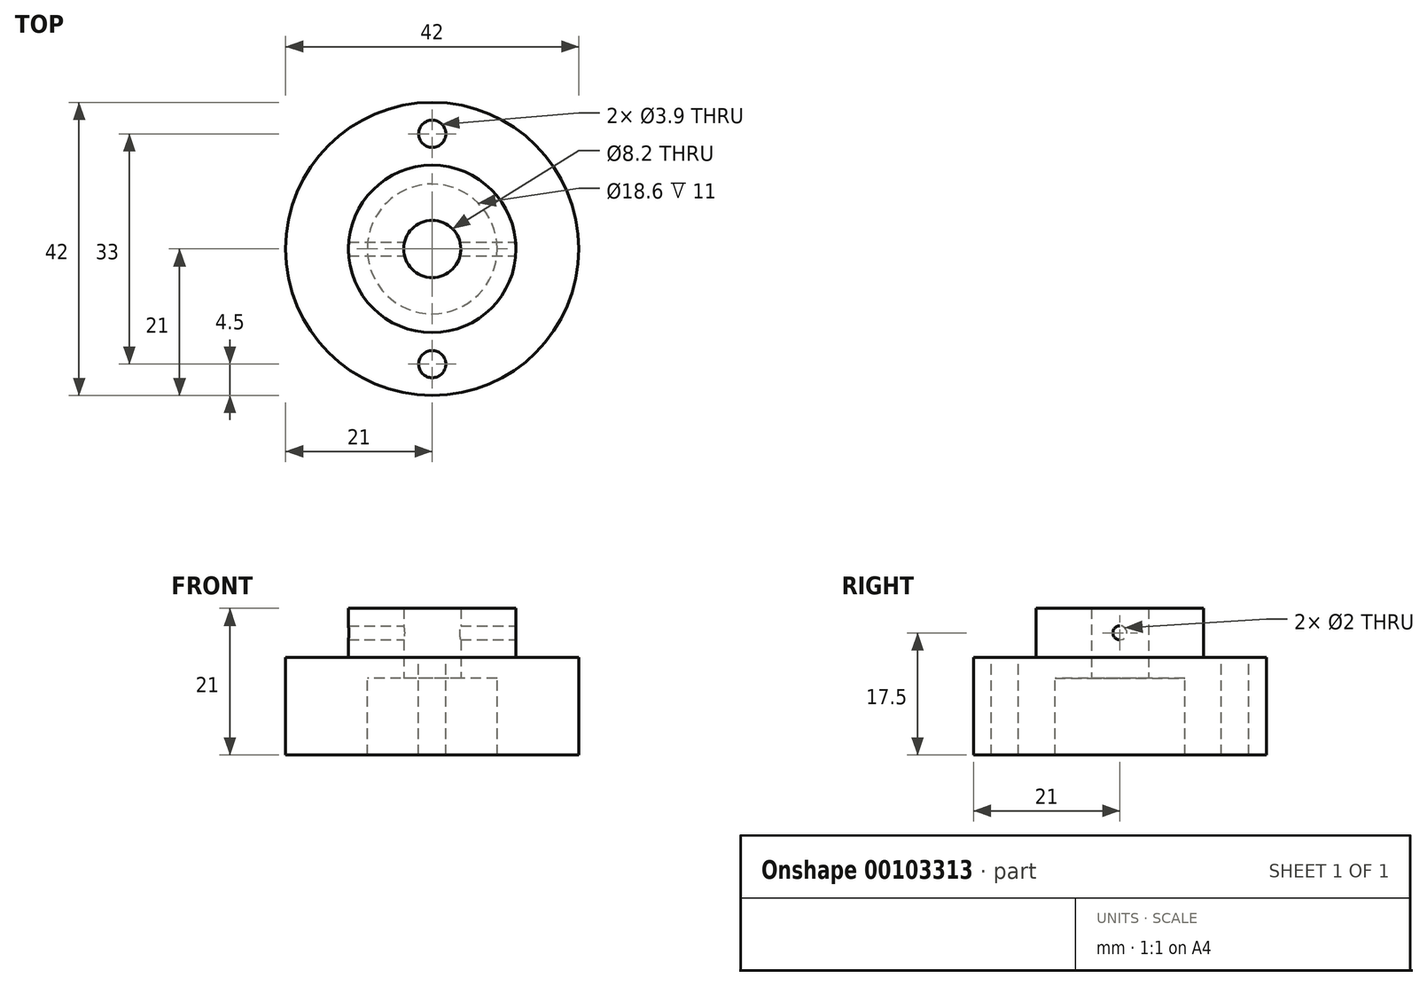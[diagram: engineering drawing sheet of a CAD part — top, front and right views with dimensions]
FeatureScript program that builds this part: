
annotation { "Feature Type Name" : "Feature", "Feature Type Description" : "" }
export const myFeature = defineFeature(function(context is Context, id is Id, definition is map)
    precondition{}
    {
        {
            var Q0;
            Q0=qCreatedBy(makeId("Top.planeOp"),FACE);
            var sketch = newSketch(context, id + "F0", { "sketchPlane" : qUnion([Q0])});
            skCircle(sketch, "E0", {"center": v(0, 0) * mm, "radius": 4.1 * mm});
            skCircle(sketch, "E1", {"center": v(0, 0) * mm, "radius": 21 * mm});
            skCircle(sketch, "E2", {"center": v(0, 0) * mm, "radius": 12 * mm});
            skSolve(sketch);
        }
        {
            var Q0;
            Q0=makeQuery(id+"F0.imprint","IMPRINT",FACE,{"disambiguationData":[TD([[makeQuery(id+"F0.imprint","IMPRINT",EDGE,{"derivedFrom":sQuery(id+"F0.wireOp",EDGE,"E1")}),1.0]])]});
            var Q1;
            Q1=makeQuery(id+"F0.imprint","IMPRINT",FACE,{"disambiguationData":[TD([[makeQuery(id+"F0.imprint","IMPRINT",EDGE,{"derivedFrom":sQuery(id+"F0.wireOp",EDGE,"E0")}),-1.0]])]});
            extrude(context, id + "F1", {"entities" : qUnion([Q0, Q1]), "depth" : 3 * mm});
        }
        {
            var Q0;
            Q0=makeQuery(id+"F0.imprint","IMPRINT",FACE,{"disambiguationData":[TD([[makeQuery(id+"F0.imprint","IMPRINT",EDGE,{"derivedFrom":sQuery(id+"F0.wireOp",EDGE,"E0")}),-1.0]])]});
            extrude(context, id + "F2", {"entities" : qUnion([Q0]), "operationType" : NewBodyOperationType.ADD, "depth" : 10 * mm});
        }
        {
            var Q0;
            Q0=qCreatedBy(makeId("Top.planeOp"),FACE);
            var sketch = newSketch(context, id + "F3", { "sketchPlane" : qUnion([Q0])});
            skCircle(sketch, "E3", {"center": v(0, 0) * mm, "radius": 9.3 * mm});
            skCircle(sketch, "E4", {"center": v(0, 0) * mm, "radius": 21 * mm});
            skSolve(sketch);
        }
        {
            var Q0;
            Q0=makeQuery(id+"F3.imprint","IMPRINT",FACE,{"disambiguationData":[TD([[makeQuery(id+"F3.imprint","IMPRINT",EDGE,{"derivedFrom":sQuery(id+"F3.wireOp",EDGE,"E3")}),-1.0]])]});
            extrude(context, id + "F4", {"entities" : qUnion([Q0]), "operationType" : NewBodyOperationType.ADD, "oppositeDirection" : true, "depth" : 11 * mm});
        }
        {
            var Q0;
            Q0=makeQuery(id+"F1.opExtrude","CAP_FACE",FACE,{"disambiguationData":[OSD([sQuery(id+"F0.wireOp",EDGE,"E0"),sQuery(id+"F0.wireOp",EDGE,"E1")])],"isStart":false});
            var sketch = newSketch(context, id + "F5", { "sketchPlane" : qUnion([Q0])});
            skCircle(sketch, "E5", {"center": v(0, 16.5) * mm, "radius": 1.95 * mm});
            skCircle(sketch, "E6", {"center": v(0, -16.5) * mm, "radius": 1.95 * mm});
            skSolve(sketch);
        }
        {
            var Q0;
            Q0=makeQuery(id+"F5.imprint","IMPRINT",FACE,{"disambiguationData":[TD([[makeQuery(id+"F5.imprint","IMPRINT",EDGE,{"derivedFrom":sQuery(id+"F5.wireOp",EDGE,"E5")}),1.0]])]});
            var Q1;
            Q1=makeQuery(id+"F5.imprint","IMPRINT",FACE,{"disambiguationData":[TD([[makeQuery(id+"F5.imprint","IMPRINT",EDGE,{"derivedFrom":sQuery(id+"F5.wireOp",EDGE,"E6")}),1.0]])]});
            var Q2;
            Q2=makeQuery(id+"F4.opExtrude","CAP_FACE",FACE,{"disambiguationData":[OSD([sQuery(id+"F3.wireOp",EDGE,"E3"),sQuery(id+"F3.wireOp",EDGE,"E4")])],"isStart":false});
            extrude(context, id + "F6", {"entities" : qUnion([Q0, Q1]), "operationType" : NewBodyOperationType.REMOVE, "endBound" : BoundingType.UP_TO_SURFACE, "oppositeDirection" : true, "endBoundEntityFace" : qUnion([Q2]), "depth" : 25 * mm});
        }
        {
            var Q0;
            Q0=qCreatedBy(makeId("Right.planeOp"),FACE);
            var sketch = newSketch(context, id + "F7", { "sketchPlane" : qUnion([Q0])});
            skCircle(sketch, "E7", {"center": v(0, 6.5) * mm, "radius": 1 * mm});
            skSolve(sketch);
        }
        {
            var Q0;
            Q0=makeQuery(id+"F7.imprint","IMPRINT",FACE,{"disambiguationData":[TD([[makeQuery(id+"F7.imprint","IMPRINT",EDGE,{"derivedFrom":sQuery(id+"F7.wireOp",EDGE,"E7")}),1.0]])]});
            extrude(context, id + "F8", {"entities" : qUnion([Q0]), "operationType" : NewBodyOperationType.REMOVE, "endBound" : BoundingType.SYMMETRIC, "oppositeDirection" : true, "depth" : 25 * mm});
        }
    });
